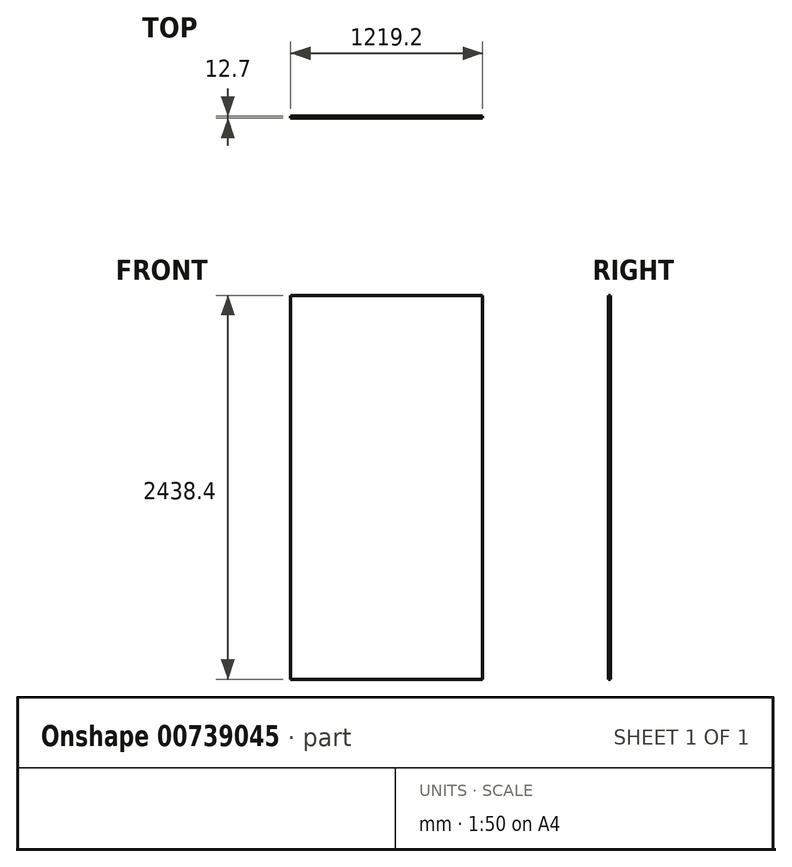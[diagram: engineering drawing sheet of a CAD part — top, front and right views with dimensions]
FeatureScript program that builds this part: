
annotation { "Feature Type Name" : "Feature", "Feature Type Description" : "" }
export const myFeature = defineFeature(function(context is Context, id is Id, definition is map)
    precondition{}
    {
        {
            var Q0;
            Q0=qCreatedBy(makeId("Front.planeOp"),FACE);
            var sketch = newSketch(context, id + "F0", { "sketchPlane" : qUnion([Q0])});
            skLineSegment(sketch, "E0.bottom", {"start": v(0, 0) * mm, "end": v(1219.2, 0) * mm});
            skLineSegment(sketch, "E0.top", {"start": v(0, 2438.4) * mm, "end": v(1219.2, 2438.4) * mm});
            skLineSegment(sketch, "E0.left", {"start": v(0, 0) * mm, "end": v(0, 2438.4) * mm});
            skLineSegment(sketch, "E0.right", {"start": v(1219.2, 0) * mm, "end": v(1219.2, 2438.4) * mm});
            skSolve(sketch);
        }
        {
            var Q0;
            Q0=makeQuery(id+"F0.imprint","IMPRINT",FACE,{"disambiguationData":[TD([[makeQuery(id+"F0.imprint","IMPRINT",EDGE,{"derivedFrom":sQuery(id+"F0.wireOp",EDGE,"E0.bottom")}),1.0]])]});
            extrude(context, id + "F1", {"entities" : qUnion([Q0]), "depth" : 12.7 * mm, "offsetDistance" : 25.4 * mm});
        }
    });
